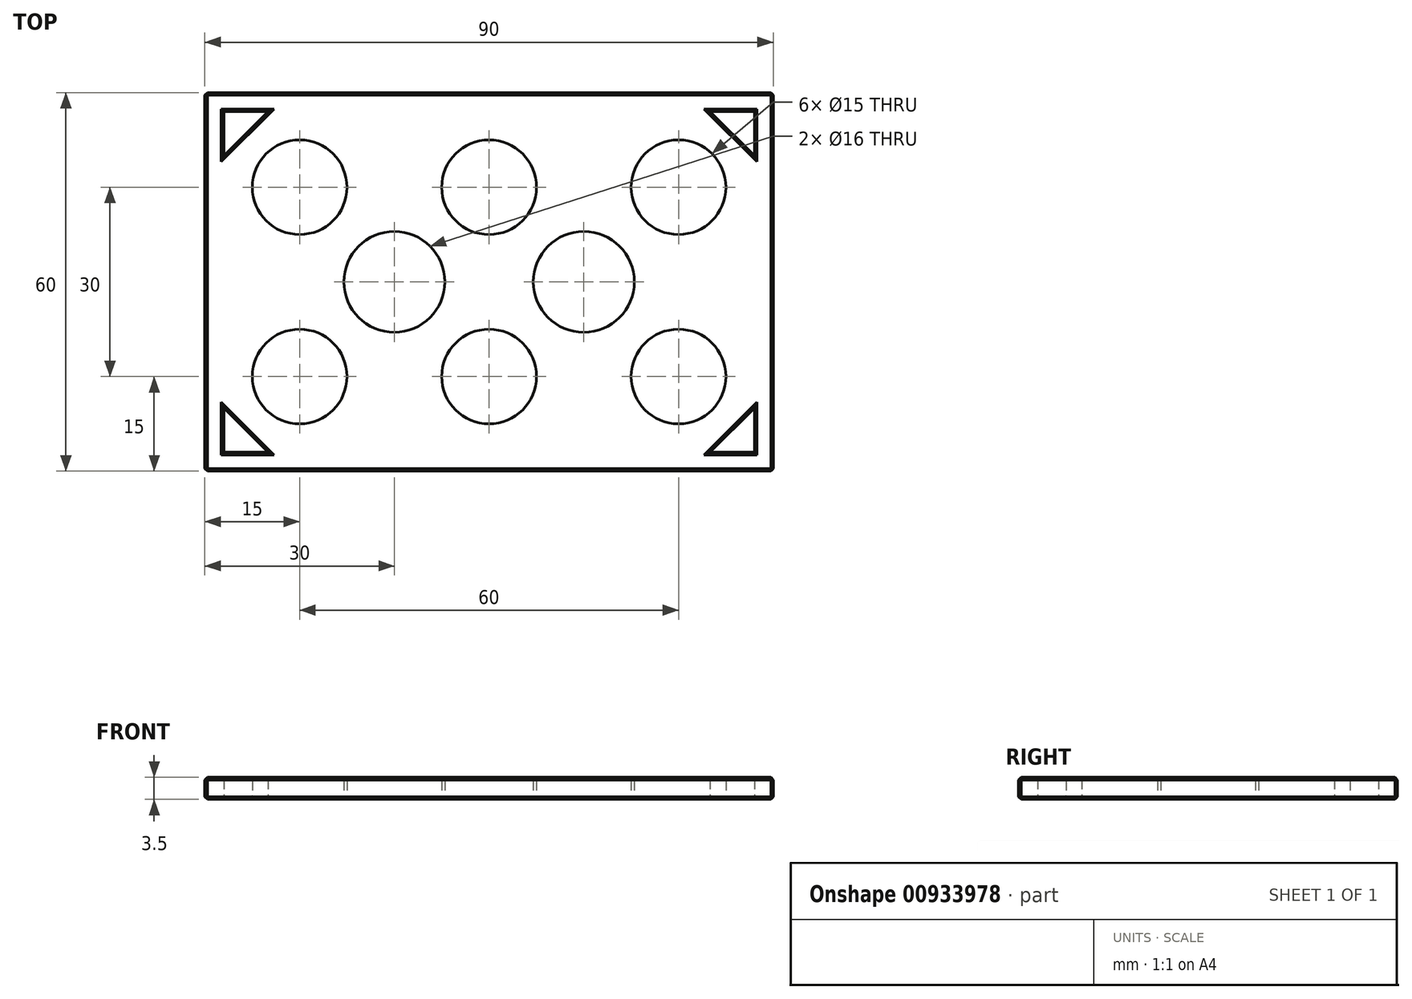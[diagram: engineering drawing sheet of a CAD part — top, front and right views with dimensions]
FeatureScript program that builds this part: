
annotation { "Feature Type Name" : "Feature", "Feature Type Description" : "" }
export const myFeature = defineFeature(function(context is Context, id is Id, definition is map)
    precondition{}
    {
        {
            var Q0;
            Q0=qCreatedBy(makeId("Top.planeOp"),FACE);
            var sketch = newSketch(context, id + "F0", { "sketchPlane" : qUnion([Q0])});
            skLineSegment(sketch, "E0.bottom", {"start": v(-45, 30) * mm, "end": v(45, 30) * mm});
            skLineSegment(sketch, "E0.top", {"start": v(-45, -30) * mm, "end": v(45, -30) * mm});
            skLineSegment(sketch, "E0.left", {"start": v(-45, 30) * mm, "end": v(-45, -30) * mm});
            skLineSegment(sketch, "E0.right", {"start": v(45, 30) * mm, "end": v(45, -30) * mm});
            skPoint(sketch, "E1", {"position": v(45, 0) * mm});
            skPoint(sketch, "E2", {"position": v(0, -30) * mm});
            skSolve(sketch);
        }
        {
            var Q0;
            Q0 = qSketchRegion(id + "F0", true);
            extrude(context, id + "F1", {"entities" : qUnion([Q0]), "depth" : 3.5 * mm, "offsetDistance" : 25 * mm});
        }
        {
            var Q0;
            Q0=qCreatedBy(makeId("Top.planeOp"),FACE);
            var sketch = newSketch(context, id + "F2", { "sketchPlane" : qUnion([Q0])});
            skCircle(sketch, "E3", {"center": v(0, 15) * mm, "radius": 7.5 * mm});
            skCircle(sketch, "E4", {"center": v(30, 15) * mm, "radius": 7.5 * mm});
            skCircle(sketch, "E5", {"center": v(15, 0) * mm, "radius": 8 * mm});
            skCircle(sketch, "E6.MirrorC", {"center": v(-30, 15) * mm, "radius": 7.5 * mm});
            skCircle(sketch, "E7.MirrorC", {"center": v(30, -15) * mm, "radius": 7.5 * mm});
            skCircle(sketch, "E8.MirrorC", {"center": v(0, -15) * mm, "radius": 7.5 * mm});
            skCircle(sketch, "E9.MirrorC", {"center": v(-30, -15) * mm, "radius": 7.5 * mm});
            skCircle(sketch, "E10.MirrorC", {"center": v(-15, 0) * mm, "radius": 8 * mm});
            skSolve(sketch);
        }
        {
            var Q0;
            Q0 = qSketchRegion(id + "F2", true);
            extrude(context, id + "F3", {"entities" : qUnion([Q0]), "operationType" : NewBodyOperationType.REMOVE, "endBound" : BoundingType.UP_TO_NEXT, "depth" : 25 * mm, "offsetDistance" : 25 * mm});
        }
        {
            var Q0;
            Q0=qCreatedBy(makeId("Top.planeOp"),FACE);
            var sketch = newSketch(context, id + "F4", { "sketchPlane" : qUnion([Q0])});
            skLineSegment(sketch, "E11.bottom", {"start": v(-42, 27) * mm, "end": v(-35, 27) * mm});
            skLineSegment(sketch, "E11.left", {"start": v(-42, 27) * mm, "end": v(-42, 20) * mm});
            skLineSegment(sketch, "E12", {"start": v(-42, 20) * mm, "end": v(-35, 27) * mm});
            skLineSegment(sketch, "E13.MirrorCS", {"start": v(42, 20) * mm, "end": v(35, 27) * mm});
            skLineSegment(sketch, "E14.MirrorCS", {"start": v(42, 27) * mm, "end": v(35, 27) * mm});
            skLineSegment(sketch, "E15.MirrorCS", {"start": v(42, 27) * mm, "end": v(42, 20) * mm});
            skLineSegment(sketch, "E16.MirrorCS", {"start": v(-42, -20) * mm, "end": v(-35, -27) * mm});
            skLineSegment(sketch, "E17.MirrorCS", {"start": v(-42, -27) * mm, "end": v(-35, -27) * mm});
            skLineSegment(sketch, "E18.MirrorCS", {"start": v(-42, -27) * mm, "end": v(-42, -20) * mm});
            skLineSegment(sketch, "E19.MirrorCS", {"start": v(42, -20) * mm, "end": v(35, -27) * mm});
            skLineSegment(sketch, "E20.MirrorCS", {"start": v(42, -27) * mm, "end": v(42, -20) * mm});
            skLineSegment(sketch, "E21.MirrorCS", {"start": v(42, -27) * mm, "end": v(35, -27) * mm});
            skSolve(sketch);
        }
        {
            var Q0;
            Q0 = qSketchRegion(id + "F4", true);
            extrude(context, id + "F5", {"entities" : qUnion([Q0]), "operationType" : NewBodyOperationType.REMOVE, "endBound" : BoundingType.UP_TO_NEXT, "depth" : 25 * mm, "offsetDistance" : 25 * mm});
        }
        {
            var Q0;
            Q0=makeQuery(id+"F3.boolean.opBoolean","COPY",FACE,{"derivedFrom":makeQuery(id+"F3.opExtrude","SWEPT_FACE",FACE,{"disambiguationData":[OSD([sQuery(id+"F2.wireOp",EDGE,"E6.MirrorC")])]})});
            var Q1;
            Q1=makeQuery(id+"F3.boolean.opBoolean","COPY",FACE,{"derivedFrom":makeQuery(id+"F3.opExtrude","SWEPT_FACE",FACE,{"disambiguationData":[OSD([sQuery(id+"F2.wireOp",EDGE,"E3")])]})});
            var Q2;
            Q2=makeQuery(id+"F3.boolean.opBoolean","COPY",FACE,{"derivedFrom":makeQuery(id+"F3.opExtrude","SWEPT_FACE",FACE,{"disambiguationData":[OSD([sQuery(id+"F2.wireOp",EDGE,"E4")])]})});
            var Q3;
            Q3=makeQuery(id+"F3.boolean.opBoolean","COPY",FACE,{"derivedFrom":makeQuery(id+"F3.opExtrude","SWEPT_FACE",FACE,{"disambiguationData":[OSD([sQuery(id+"F2.wireOp",EDGE,"E10.MirrorC")])]})});
            var Q4;
            Q4=makeQuery(id+"F3.boolean.opBoolean","COPY",FACE,{"derivedFrom":makeQuery(id+"F3.opExtrude","SWEPT_FACE",FACE,{"disambiguationData":[OSD([sQuery(id+"F2.wireOp",EDGE,"E9.MirrorC")])]})});
            var Q5;
            Q5=makeQuery(id+"F3.boolean.opBoolean","COPY",FACE,{"derivedFrom":makeQuery(id+"F3.opExtrude","SWEPT_FACE",FACE,{"disambiguationData":[OSD([sQuery(id+"F2.wireOp",EDGE,"E8.MirrorC")])]})});
            var Q6;
            Q6=makeQuery(id+"F3.boolean.opBoolean","COPY",FACE,{"derivedFrom":makeQuery(id+"F3.opExtrude","SWEPT_FACE",FACE,{"disambiguationData":[OSD([sQuery(id+"F2.wireOp",EDGE,"E7.MirrorC")])]})});
            var Q7;
            Q7=makeQuery(id+"F3.boolean.opBoolean","COPY",FACE,{"derivedFrom":makeQuery(id+"F3.opExtrude","SWEPT_FACE",FACE,{"disambiguationData":[OSD([sQuery(id+"F2.wireOp",EDGE,"E5")])]})});
            fillet(context, id + "F6", {"entities" : qUnion([Q0, Q1, Q2, Q3, Q4, Q5, Q6, Q7]), "radius" : 0.6 * mm, "tangentPropagation" : true, "allowEdgeOverflow" : false});
        }
        {
            var Q0;
            Q0=makeQuery(id+"F1.opExtrude","SWEPT_FACE",FACE,{"disambiguationData":[OSD([sQuery(id+"F0.wireOp",EDGE,"E0.top")])]});
            var Q1;
            Q1=makeQuery(id+"F1.opExtrude","SWEPT_FACE",FACE,{"disambiguationData":[OSD([sQuery(id+"F0.wireOp",EDGE,"E0.right")])]});
            var Q2;
            Q2=makeQuery(id+"F1.opExtrude","SWEPT_FACE",FACE,{"disambiguationData":[OSD([sQuery(id+"F0.wireOp",EDGE,"E0.bottom")])]});
            var Q3;
            Q3=makeQuery(id+"F1.opExtrude","SWEPT_FACE",FACE,{"disambiguationData":[OSD([sQuery(id+"F0.wireOp",EDGE,"E0.left")])]});
            var Q4;
            Q4=makeQuery(id+"F1.opExtrude","CAP_FACE",FACE,{"disambiguationData":[OSD([sQuery(id+"F0.wireOp",EDGE,"E0.bottom"),sQuery(id+"F0.wireOp",EDGE,"E0.top"),sQuery(id+"F0.wireOp",EDGE,"E0.left"),sQuery(id+"F0.wireOp",EDGE,"E0.right")])],"isStart":false});
            chamfer(context, id + "F7", {"entities" : qUnion([Q0, Q1, Q2, Q3, Q4]), "width" : 0.4 * mm, "tangentPropagation" : true});
        }
    });
